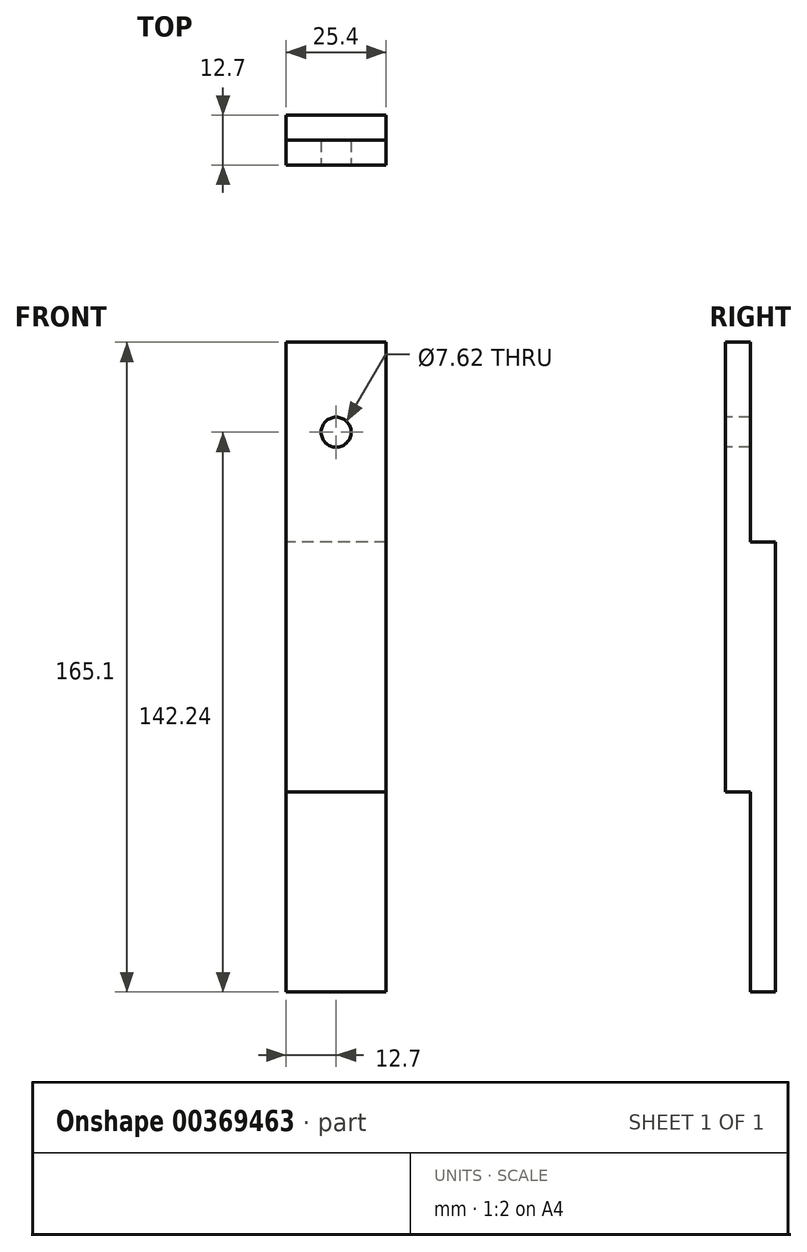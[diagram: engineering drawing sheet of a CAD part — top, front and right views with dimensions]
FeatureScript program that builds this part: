
annotation { "Feature Type Name" : "Feature", "Feature Type Description" : "" }
export const myFeature = defineFeature(function(context is Context, id is Id, definition is map)
    precondition{}
    {
        {
            var Q0;
            Q0=qCreatedBy(makeId("Front.planeOp"),FACE);
            var sketch = newSketch(context, id + "F0", { "sketchPlane" : qUnion([Q0])});
            skLineSegment(sketch, "E0.bottom", {"start": v(0, 0) * mm, "end": v(25.4, 0) * mm});
            skLineSegment(sketch, "E0.top", {"start": v(0, 165.1) * mm, "end": v(25.4, 165.1) * mm});
            skLineSegment(sketch, "E0.left", {"start": v(0, 0) * mm, "end": v(0, 165.1) * mm});
            skLineSegment(sketch, "E0.right", {"start": v(25.4, 0) * mm, "end": v(25.4, 165.1) * mm});
            skSolve(sketch);
        }
        {
            var Q0;
            Q0=qSketchRegion(id+"F0",true);
            extrude(context, id + "F1", {"entities" : qUnion([Q0]), "depth" : 12.7 * mm});
        }
        {
            var Q0;
            Q0=makeQuery(id+"F1.opExtrude","CAP_FACE",FACE,{"disambiguationData":[OSD([sQuery(id+"F0.wireOp",EDGE,"E0.bottom"),sQuery(id+"F0.wireOp",EDGE,"E0.top"),sQuery(id+"F0.wireOp",EDGE,"E0.left"),sQuery(id+"F0.wireOp",EDGE,"E0.right")])],"isStart":false});
            var sketch = newSketch(context, id + "F2", { "sketchPlane" : qUnion([Q0])});
            skLineSegment(sketch, "E1.bottom", {"start": v(0, 0) * mm, "end": v(25.4, 0) * mm});
            skLineSegment(sketch, "E1.top", {"start": v(0, 50.8) * mm, "end": v(25.4, 50.8) * mm});
            skLineSegment(sketch, "E1.left", {"start": v(0, 0) * mm, "end": v(0, 50.8) * mm});
            skLineSegment(sketch, "E1.right", {"start": v(25.4, 0) * mm, "end": v(25.4, 50.8) * mm});
            skSolve(sketch);
        }
        {
            var Q0;
            Q0=makeQuery(id+"F2.imprint","IMPRINT",FACE,{"disambiguationData":[TD([[makeQuery(id+"F2.imprint","IMPRINT",EDGE,{"derivedFrom":sQuery(id+"F2.wireOp",EDGE,"E1.bottom")}),1.0]])]});
            extrude(context, id + "F3", {"entities" : qUnion([Q0]), "operationType" : NewBodyOperationType.ADD, "oppositeDirection" : true, "depth" : 6.35 * mm});
        }
        {
            var Q0;
            Q0=qSketchRegion(id+"F2",true);
            extrude(context, id + "F4", {"entities" : qUnion([Q0]), "operationType" : NewBodyOperationType.REMOVE, "oppositeDirection" : true, "depth" : 6.35 * mm});
        }
        {
            var Q0;
            Q0=makeQuery(id+"F1.opExtrude","CAP_FACE",FACE,{"disambiguationData":[OSD([sQuery(id+"F0.wireOp",EDGE,"E0.bottom"),sQuery(id+"F0.wireOp",EDGE,"E0.top"),sQuery(id+"F0.wireOp",EDGE,"E0.left"),sQuery(id+"F0.wireOp",EDGE,"E0.right")])],"isStart":true});
            var sketch = newSketch(context, id + "F5", { "sketchPlane" : qUnion([Q0])});
            skLineSegment(sketch, "E2.bottom", {"start": v(-25.4, 165.1) * mm, "end": v(0, 165.1) * mm});
            skLineSegment(sketch, "E2.top", {"start": v(-25.4, 114.3) * mm, "end": v(0, 114.3) * mm});
            skLineSegment(sketch, "E2.left", {"start": v(-25.4, 165.1) * mm, "end": v(-25.4, 114.3) * mm});
            skLineSegment(sketch, "E2.right", {"start": v(0, 165.1) * mm, "end": v(0, 114.3) * mm});
            skSolve(sketch);
        }
        {
            var Q0;
            Q0=makeQuery(id+"F5.imprint","IMPRINT",FACE,{"disambiguationData":[TD([[makeQuery(id+"F5.imprint","IMPRINT",EDGE,{"derivedFrom":sQuery(id+"F5.wireOp",EDGE,"E2.bottom")}),1.0]])]});
            extrude(context, id + "F6", {"entities" : qUnion([Q0]), "operationType" : NewBodyOperationType.REMOVE, "oppositeDirection" : true, "depth" : 6.35 * mm});
        }
        {
            var Q0;
            Q0=makeQuery(id+"F1.opExtrude","CAP_FACE",FACE,{"disambiguationData":[OSD([sQuery(id+"F0.wireOp",EDGE,"E0.bottom"),sQuery(id+"F0.wireOp",EDGE,"E0.top"),sQuery(id+"F0.wireOp",EDGE,"E0.left"),sQuery(id+"F0.wireOp",EDGE,"E0.right")])],"isStart":false});
            var sketch = newSketch(context, id + "F7", { "sketchPlane" : qUnion([Q0])});
            skCircle(sketch, "E3", {"center": v(12.7, 142.24) * mm, "radius": 3.81 * mm});
            skSolve(sketch);
        }
        {
            var Q0;
            Q0=makeQuery(id+"F7.imprint","IMPRINT",FACE,{"disambiguationData":[TD([[makeQuery(id+"F7.imprint","IMPRINT",EDGE,{"derivedFrom":sQuery(id+"F7.wireOp",EDGE,"E3")}),1.0]])]});
            extrude(context, id + "F8", {"entities" : qUnion([Q0]), "operationType" : NewBodyOperationType.REMOVE, "oppositeDirection" : true, "depth" : 25.4 * mm});
        }
    });
